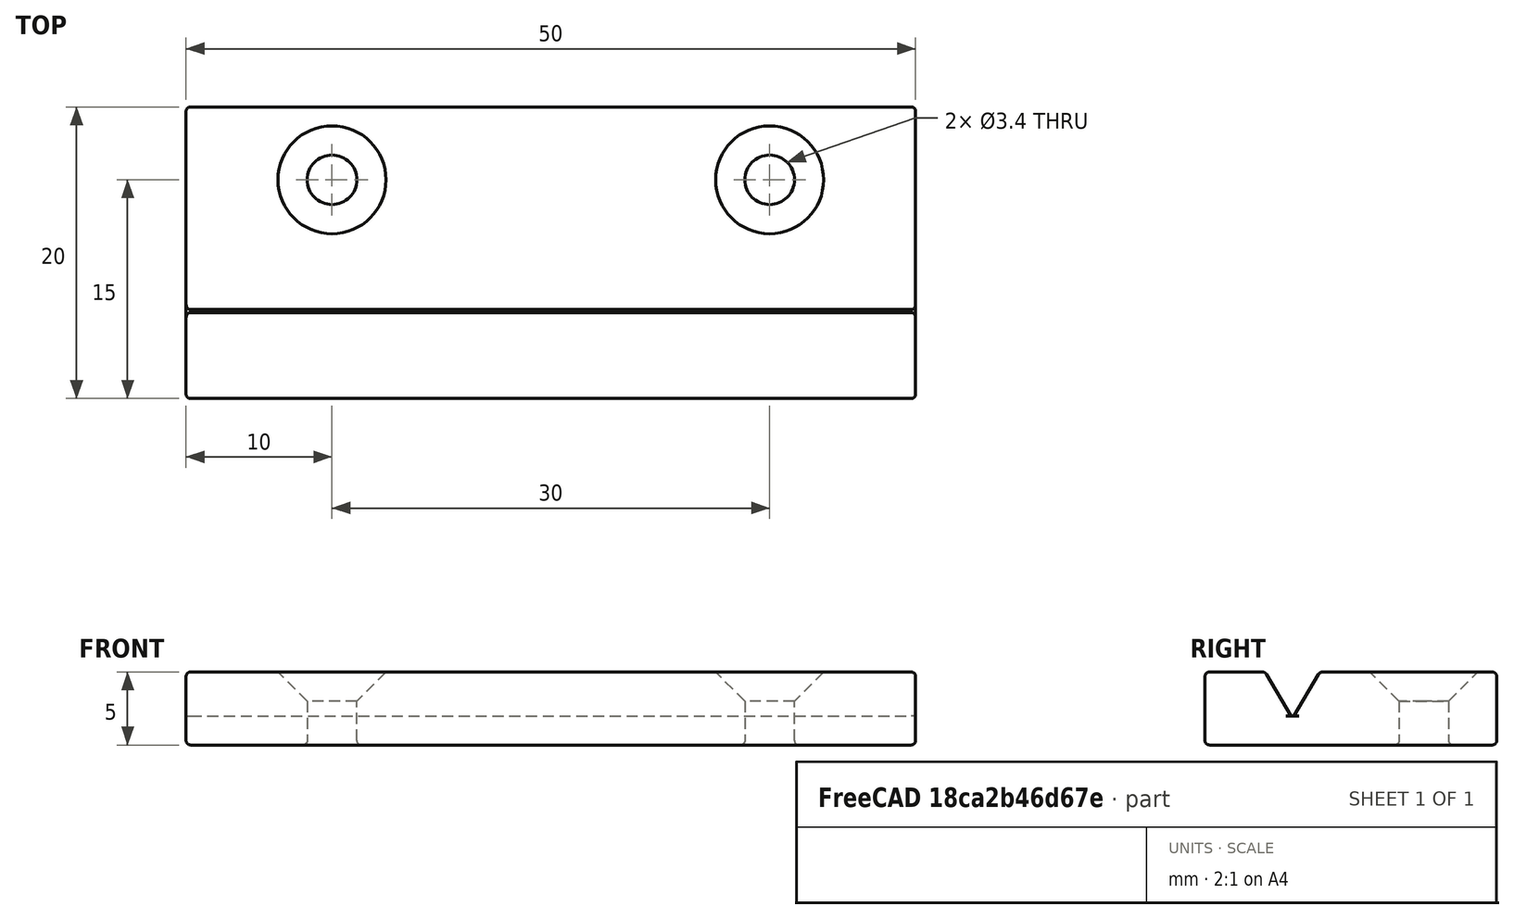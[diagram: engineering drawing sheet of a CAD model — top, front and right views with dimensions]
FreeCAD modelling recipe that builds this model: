
FCSTD DOCUMENT  (FreeCAD 0.20R24992 (Git))
Label: GegenlagerVaccum
License: All rights reserved
LicenseURL: http://en.wikipedia.org/wiki/All_rights_reserved
objects: Part::Cut×3, Part::Box×2, Part::Chamfer×2, Part::Cylinder×2, Part::Fillet×1
note: 10 computed .brp shape members not serialized (recipe doc carries the construction recipe); baked Part::Feature solids carry a one-line shape summary decoded from their .brp

FEATURE [Part::Box] Box  label="Cube"
  AttacherType = Attacher::AttachEngine3D
  Height = 5
  Length = 50
  Placement = pos=(0,0,2) rot=(0,0,1;0rad)
  Width = 6
FEATURE [Part::Chamfer] Chamfer
  Base = -> Box
  Edges = 2 edges: [Edge9 r1=4.9 r2=2.9,Edge11 r1=4.9 r2=2.9]
  Placement = pos=(0,3,0) rot=(0,0,1;0rad)
FEATURE [Part::Box] Box001  label="Cube001"
  AttacherType = Attacher::AttachEngine3D
  Height = 5
  Length = 50
  Width = 20
FEATURE [Part::Cylinder] Cylinder
  Angle = 360
  AttacherType = Attacher::AttachEngine3D
  FirstAngle = 0
  Height = 10
  Placement = pos=(10,15,0) rot=(0,0,1;0rad)
  Radius = 1.7
  SecondAngle = 0
FEATURE [Part::Cylinder] Cylinder001
  Angle = 360
  AttacherType = Attacher::AttachEngine3D
  FirstAngle = 0
  Height = 10
  Placement = pos=(40,15,0) rot=(0,0,1;0rad)
  Radius = 1.7
  SecondAngle = 0
FEATURE [Part::Cut] Cut
  Base = -> Box001
  Tool = -> Chamfer
FEATURE [Part::Cut] Cut001
  Base = -> Cut
  Tool = -> Cylinder001
FEATURE [Part::Cut] Cut002
  Base = -> Cut001
  Tool = -> Cylinder
FEATURE [Part::Chamfer] Chamfer001
  Base = -> Cut002
  Edges = 2 edges r=2: [Edge20,Edge21]
FEATURE [Part::Fillet] Fillet
  Base = -> Chamfer001
  Edges = 22 edges r=0.3: [Edge2,Edge3,Edge4,Edge5,Edge9,Edge10,Edge12,Edge13,Edge14,Edge15,Edge17,Edge18,Edge19,Edge20,Edge21,Edge23,Edge24,Edge28,Edge29,Edge30,Edge32,Edge33]
